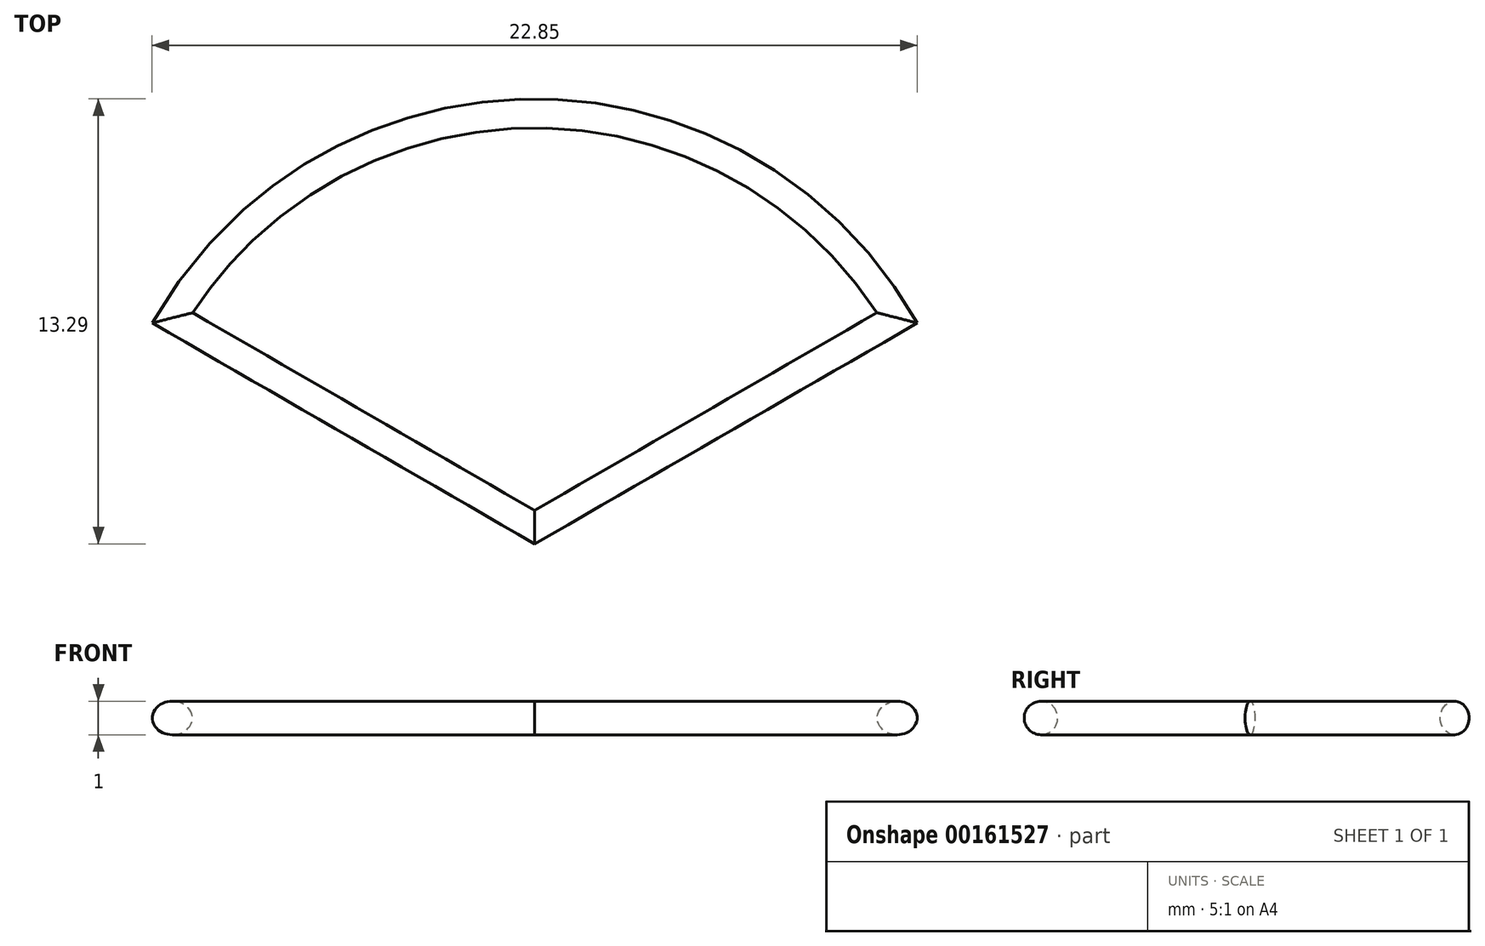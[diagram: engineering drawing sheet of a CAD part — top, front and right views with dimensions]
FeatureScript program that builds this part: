
annotation { "Feature Type Name" : "Feature", "Feature Type Description" : "" }
export const myFeature = defineFeature(function(context is Context, id is Id, definition is map)
    precondition{}
    {
        {
            var Q0;
            Q0=qCreatedBy(makeId("Top.planeOp"),FACE);
            var sketch = newSketch(context, id + "F0", { "sketchPlane" : qUnion([Q0])});
            skLineSegment(sketch, "E0", {"start": v(0, 0) * mm, "end": v(-10.83, 6.25) * mm});
            skLineSegment(sketch, "E1", {"start": v(0, 0) * mm, "end": v(10.83, 6.25) * mm});
            skLineSegment(sketch, "E2", {"start": v(-11.01, -4.4) * mm, "end": v(13.06, -4.4) * mm, "construction": true});
            skArc(sketch, "E3", {"start": v(10.83, 6.25) * mm, "mid": v(0, 12.36) * mm, "end": v(-10.83, 6.25) * mm});
            skSolve(sketch);
        }
        {
            var Q0;
            Q0=qCreatedBy(makeId("Right.planeOp"),FACE);
            var sketch = newSketch(context, id + "F1", { "sketchPlane" : qUnion([Q0])});
            skCircle(sketch, "E4", {"center": v(0, 0) * mm, "radius": 0.5 * mm});
            skSolve(sketch);
        }
        {
            var Q0;
            Q0=makeQuery(id+"F1.imprint","IMPRINT",FACE,{"disambiguationData":[TD([[makeQuery(id+"F1.imprint","IMPRINT",EDGE,{"derivedFrom":sQuery(id+"F1.wireOp",EDGE,"E4")}),1.0]])]});
            var Q1;
            Q1=sQuery(id+"F0.wireOp",EDGE,"E0");
            var Q2;
            Q2=sQuery(id+"F0.wireOp",EDGE,"E3");
            var Q3;
            Q3=sQuery(id+"F0.wireOp",EDGE,"E1");
            sweep(context, id + "F2", {"profiles" : qUnion([Q0]), "path" : qUnion([Q1, Q2, Q3])});
        }
    });
